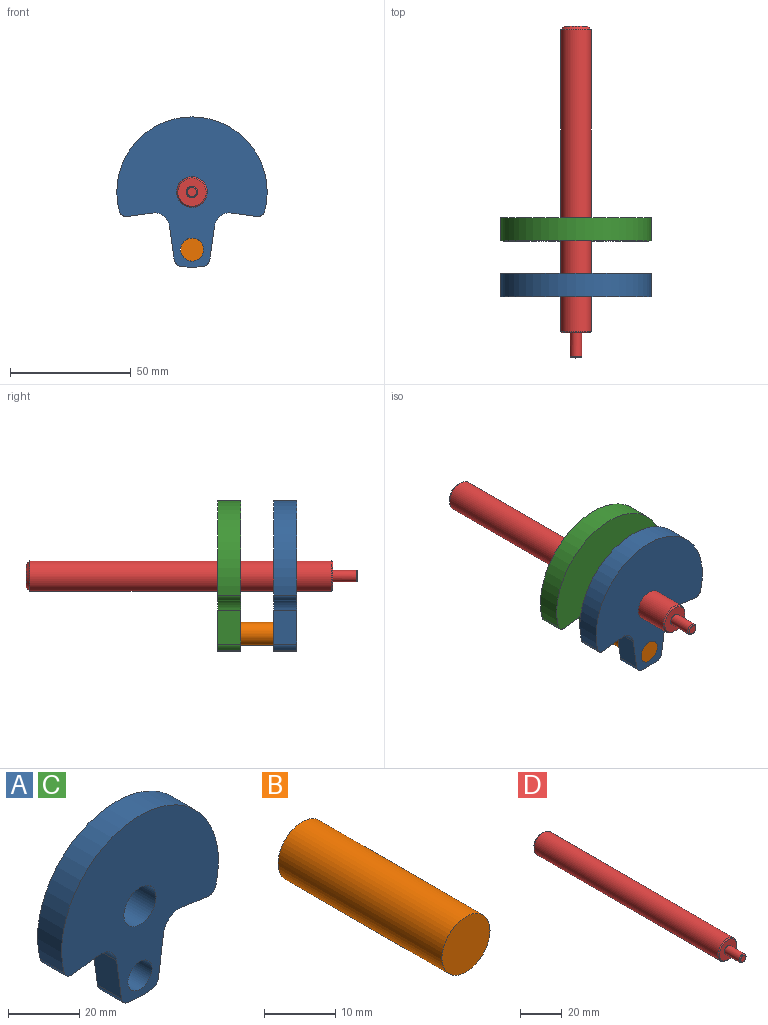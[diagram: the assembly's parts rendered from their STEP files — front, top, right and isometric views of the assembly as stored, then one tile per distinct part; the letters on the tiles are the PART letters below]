
ASSEMBLY  parts=4 mates=3
PART A: 16 faces, bbox 62.2x9.5x62.2 mm
  f0: cylinder r=3.05mm len=9.53mm, axis (0,1,0), area 37.1mm2, adj f1,f13,f14,f15
  f1: cylinder r=31.12mm len=9.59mm, axis (0,1,0), area 91.7mm2, adj f0,f2,f14,f15
  f2: cylinder r=3.05mm len=9.53mm, axis (0,1,0), area 37.1mm2, adj f1,f3,f14,f15
  f3: plane 14.07x9.53mm, normal (0.99,0,-0.14), area 135.3mm2, adj f2,f4,f14,f15
  f4: cylinder r=6.35mm len=9.53mm, axis (0,1,0), area 95mm2, adj f3,f5,f14,f15
  f5: plane 10.24x9.53mm, normal (-0.14,0,-0.99), area 98.5mm2, adj f4,f6,f14,f15
  f6: cylinder r=3.05mm len=9.53mm, axis (0,1,0), area 42.2mm2, adj f5,f7,f14,f15
  f7: cylinder r=31.12mm len=62.23mm, axis (0,1,0), area 1082.7mm2, adj f6,f8,f14,f15
  f8: cylinder r=3.05mm len=9.53mm, axis (0,1,0), area 42.2mm2, adj f7,f9,f14,f15
  f9: plane 10.24x9.53mm, normal (0.14,0,-0.99), area 98.5mm2, adj f8,f10,f14,f15
  f10: cylinder r=6.35mm len=9.53mm, axis (0,1,0), area 95mm2, adj f9,f13,f14,f15
  f11: cylinder r=4.78mm len=9.55mm, axis (0,1,0), area 285.8mm2, adj f14,f15
  f12: cylinder r=6.36mm len=12.73mm, axis (0,1,0), area 380.8mm2, adj f14,f15
  f13: plane 14.07x9.53mm, normal (-0.99,0,-0.14), area 135.3mm2, adj f0,f10,f14,f15
  f14: plane 62.23x62.23mm, normal (0,-1,0), area 2264.1mm2, adj f0,f1,f2,f3,f4,f5,f6,f7
  f15: plane 62.23x62.23mm, normal (0,1,0), area 2264.1mm2, adj f0,f1,f2,f3,f4,f5,f6,f7
PART B: 3 faces, bbox 9.5x32.5x9.5 mm
  f0: cylinder r=4.76mm len=32.51mm, axis (0,1,0), area 972.9mm2, adj f1,f2
  f1: plane 9.53x9.53mm, normal (0,-1,0), area 71.3mm2, adj f0
  f2: plane 9.53x9.53mm, normal (0,1,0), area 71.3mm2, adj f0
PART C: same geometry as A
PART D: 8 faces, bbox 12.7x137.4x12.7 mm
  f0: cylinder r=6.35mm len=124.97mm, axis (0,-1,0), area 4986mm2, adj f5,f7
  f1: plane 9.65x9.65mm, normal (0,1,0), area 73.2mm2, adj f7
  f2: plane 11.68x11.68mm, normal (0,-1,0), area 89.4mm2, adj f3,f5
  f3: cylinder r=2.38mm len=9.91mm, axis (0,1,0), area 148.2mm2, adj f2,f6
  f4: plane 3.75x3.75mm, normal (0,-1,0), area 11mm2, adj f6
  f5: cone r=5.84mm half-angle=45deg, axis (0,1,0), area 27.5mm2, adj f0,f2
  f6: cone r=1.87mm half-angle=45deg, axis (0,1,0), area 9.6mm2, adj f3,f4
  f7: cone r=6.35mm half-angle=45deg, axis (0,-1,0), area 75.7mm2, adj f0,f1
PLACE A t=(71.8,116.6,6.77)mm
PLACE B t=(84.9,139.58,29.81)mm
PLACE C t=(71.8,139.63,6.77)mm
PLACE D t=(23.55,92.08,6.77)mm
MATE fastened D.f0 <-> A.f1  axis (0,-1,0) through (23.55,92.08,6.77)mm
MATE fastened A.f1 <-> C.f1  axis (0,1,0) through (23.55,116.6,6.77)mm
MATE fastened B.f0 <-> A.f11  axis (0,-1,0) through (23.55,107.07,-17.06)mm
